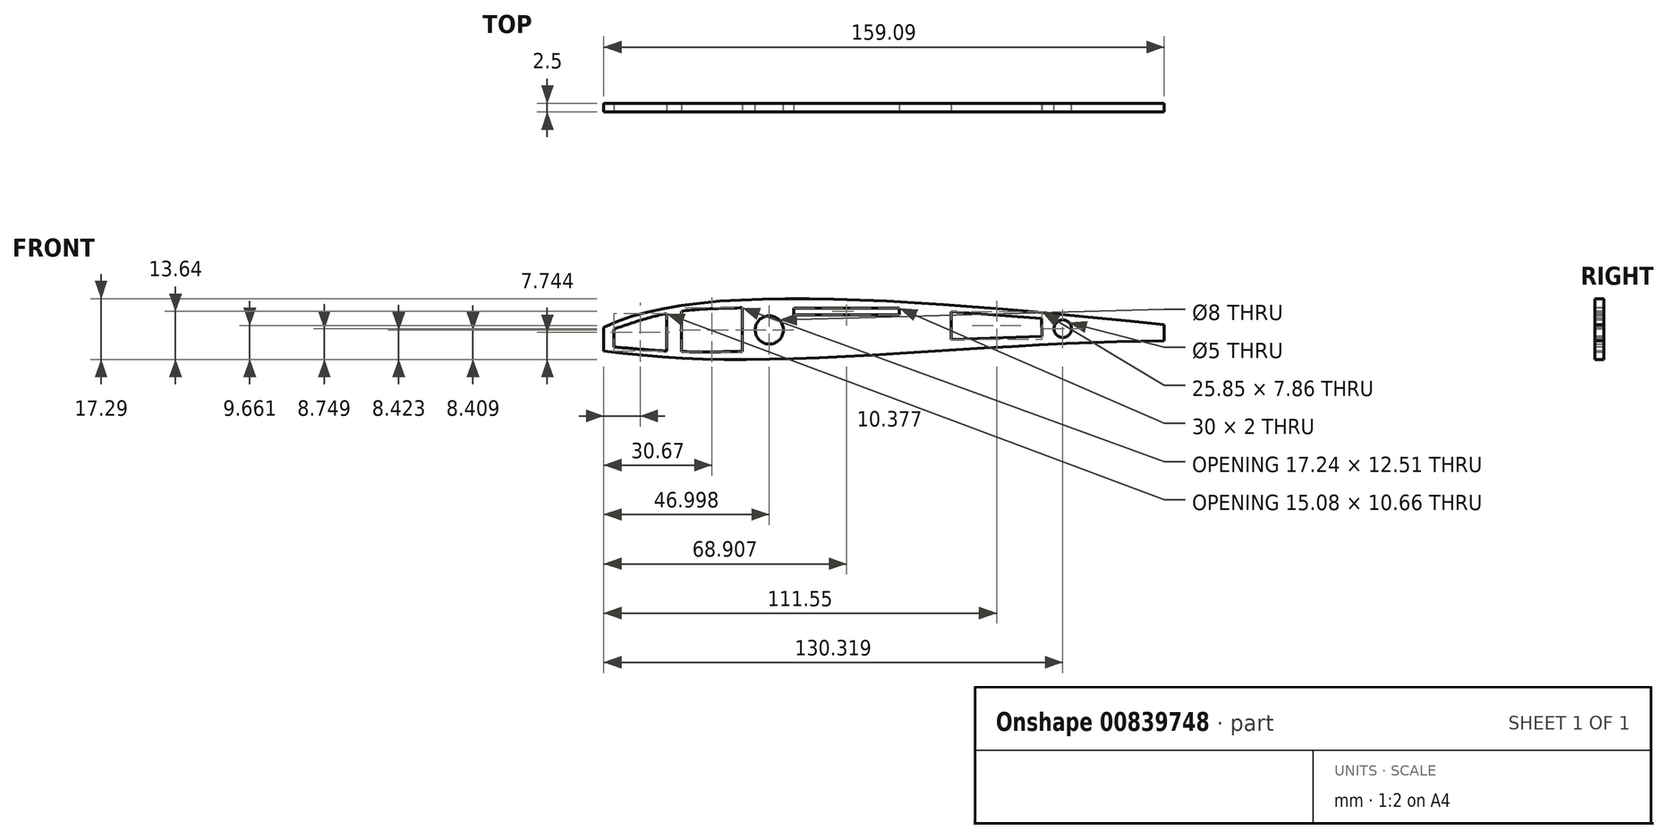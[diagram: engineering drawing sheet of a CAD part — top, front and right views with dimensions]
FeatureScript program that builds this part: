
annotation { "Feature Type Name" : "Feature", "Feature Type Description" : "" }
export const myFeature = defineFeature(function(context is Context, id is Id, definition is map)
    precondition{}
    {
        {
            var Q0;
            Q0=qCreatedBy(makeId("Front.planeOp"),FACE);
            var sketch = newSketch(context, id + "F0", { "sketchPlane" : qUnion([Q0])});
            skPoint(sketch, "E0.middle", {"position": v(0, 0) * mm});
            skLineSegment(sketch, "E1", {"start": v(-99.95, -4.05) * mm, "end": v(-99.64, -4.05) * mm});
            skFitSpline(sketch, "E2", {"points": [v(-96.98, -0.81) * mm, v(-45.24, 7.5) * mm, v(100, -4.05) * mm], "startDerivative": vector(97.58, 47.67) * mm, "endDerivative": vector(275.05, -31.29) * mm});
            skFitSpline(sketch, "E3", {"points": [v(-96.54, -7.34) * mm, v(-44.56, -9.6) * mm, v(41.7, -4.97) * mm, v(100, -4.05) * mm], "startDerivative": vector(159.07, -20.98) * mm, "endDerivative": vector(169.88, 6) * mm});
            skFitSpline(sketch, "E4", {"points": [v(-96.54, -7.34) * mm, v(-101.41, -5) * mm, v(-96.98, -0.81) * mm], "startDerivative": vector(-18.7, 3.9) * mm, "endDerivative": vector(17.62, 9.13) * mm});
            skArc(sketch, "E5.trimOffspring", {"start": v(-97.54, -7.12) * mm, "mid": v(-97.05, -7.27) * mm, "end": v(-96.54, -7.34) * mm});
            skFitSpline(sketch, "E6", {"points": [v(-96.34, -1.64) * mm, v(-45.34, 6.27) * mm, v(86.1, -3.38) * mm], "startDerivative": vector(82.57, 38.4) * mm, "endDerivative": vector(239.73, -24.74) * mm});
            skFitSpline(sketch, "E7", {"points": [v(-97.38, -6.05) * mm, v(-44.49, -7.96) * mm, v(41.39, -3.9) * mm, v(86.1, -3.38) * mm], "startDerivative": vector(144.05, -26.77) * mm, "endDerivative": vector(139.27, -2.3) * mm});
            skFitSpline(sketch, "E8", {"points": [v(-97.38, -6.05) * mm, v(-99.95, -4.56) * mm, v(-96.34, -1.64) * mm], "startDerivative": vector(-8.62, 1.03) * mm, "endDerivative": vector(10.24, 4.38) * mm});
            skSolve(sketch);
        }
        {
            var Q0;
            Q0=qCreatedBy(makeId("Front.planeOp"),FACE);
            var sketch = newSketch(context, id + "F1", { "sketchPlane" : qUnion([Q0])});
            skLineSegment(sketch, "E9", {"start": v(-109.84, -5.04) * mm, "end": v(108.45, -3.99) * mm});
            skCircle(sketch, "E10", {"center": v(-49.54, -1.37) * mm, "radius": 4 * mm});
            skCircle(sketch, "E11", {"center": v(33.78, -1.03) * mm, "radius": 2.5 * mm});
            skSolve(sketch);
        }
        {
            var Q0;
            {var subQ0=sQuery(id+"F0.wireOp",EDGE,"E6");Q0=makeQuery(id+"F0.imprint","IMPRINT",FACE,{"disambiguationData":[TD([[makeQuery(id+"F0.imprint","IMPRINT",EDGE,{"derivedFrom":subQ0}),-1.0]])]});}
            var Q1;
            {var subQ1=sQuery(id+"F0.wireOp",EDGE,"E2");Q1=makeQuery(id+"F0.imprint","IMPRINT",FACE,{"disambiguationData":[TD([[makeQuery(id+"F0.imprint","IMPRINT",EDGE,{"derivedFrom":subQ1}),-1.0]])]});}
            var Q2;
            Q2=makeQuery(id+"F1.imprint","IMPRINT",FACE,{"disambiguationData":[TD([[makeQuery(id+"F1.imprint","IMPRINT",EDGE,{"derivedFrom":sQuery(id+"F1.wireOp",EDGE,"E11")}),1.0]])]});
            var Q3;
            {var subQ0=sQuery(id+"F1.wireOp",EDGE,"E10");var subQ1=sQuery(id+"F1.wireOp",EDGE,"E9");var subQ2=makeQuery(id+"F1.imprint","INTERSECT",VERTEX,{"disambiguationData":[OD(0.0)],"derivedFrom":[subQ1,subQ0]});Q3=makeQuery(id+"F1.imprint","IMPRINT",FACE,{"disambiguationData":[TD([[makeQuery(id+"F1.imprint","IMPRINT",EDGE,{"disambiguationData":[TD([[subQ2,-1.0]])],"derivedFrom":subQ1}),1.0]])]});}
            var Q4;
            {var subQ0=sQuery(id+"F1.wireOp",EDGE,"E10");var subQ1=sQuery(id+"F1.wireOp",EDGE,"E9");var subQ2=makeQuery(id+"F1.imprint","INTERSECT",VERTEX,{"disambiguationData":[OD(0.0)],"derivedFrom":[subQ1,subQ0]});Q4=makeQuery(id+"F1.imprint","IMPRINT",FACE,{"disambiguationData":[TD([[makeQuery(id+"F1.imprint","IMPRINT",EDGE,{"disambiguationData":[TD([[subQ2,-1.0]])],"derivedFrom":subQ1}),-1.0]])]});}
            var Q5;
            {var subQ0=sQuery(id+"F0.wireOp",EDGE,"E5.trimOffspring");Q5=makeQuery(id+"F0.imprint","IMPRINT",FACE,{"disambiguationData":[TD([[makeQuery(id+"F0.imprint","IMPRINT",EDGE,{"derivedFrom":subQ0}),1.0]])]});}
            extrude(context, id + "F2", {"entities" : qUnion([Q0, Q1, Q2, Q3, Q4, Q5]), "depth" : 2.5 * mm, "offsetDistance" : 25 * mm});
        }
        {
            var Q0;
            Q0 = qSketchRegion(id + "F1", true);
            var Q1;
            Q1=sQuery(id+"F1.wireOp",EDGE,"E11");
            var Q2;
            Q2=sQuery(id+"F1.wireOp",EDGE,"E10");
            extrude(context, id + "F3", {"entities" : qUnion([Q0]), "operationType" : NewBodyOperationType.REMOVE, "surfaceEntities" : qUnion([Q1, Q2]), "depth" : 2.5 * mm, "offsetDistance" : 25 * mm});
        }
        {
            var Q0;
            Q0=makeQuery(id+"F2.opExtrude","CAP_FACE",FACE,{"disambiguationData":[OSD([sQuery(id+"F0.wireOp",EDGE,"E2"),sQuery(id+"F0.wireOp",EDGE,"E3"),sQuery(id+"F0.wireOp",EDGE,"E4"),sQuery(id+"F0.wireOp",EDGE,"E5.trimOffspring")])],"isStart":false});
            var sketch = newSketch(context, id + "F4", { "sketchPlane" : qUnion([Q0])});
            skLineSegment(sketch, "E12", {"start": v(-96.54, -0.6) * mm, "end": v(-96.54, -7.34) * mm});
            skPoint(sketch, "E13.end.orphan", {"position": v(-96.98, -7.34) * mm});
            skLineSegment(sketch, "E14", {"start": v(-57.25, 4.9) * mm, "end": v(-57.25, -7.48) * mm});
            skFitSpline(sketch, "E15", {"points": [v(-57.25, -7.48) * mm, v(-75.97, -7.48) * mm, v(-93.7, -6.2) * mm], "startDerivative": vector(-37.23, -0.66) * mm, "endDerivative": vector(-35.67, 3.25) * mm});
            skFitSpline(sketch, "E16", {"points": [v(-57.25, 4.9) * mm, v(-77.46, 3.51) * mm, v(-93.7, -1.14) * mm], "startDerivative": vector(-39.88, -0.8) * mm, "endDerivative": vector(-32.92, -11.45) * mm});
            skLineSegment(sketch, "E17", {"start": v(-93.7, -1.14) * mm, "end": v(-93.7, -6.2) * mm});
            skLineSegment(sketch, "E18", {"start": v(2.08, 3.8) * mm, "end": v(2.08, -4.05) * mm});
            skLineSegment(sketch, "E19", {"start": v(2.08, -4.05) * mm, "end": v(27.94, -3.22) * mm});
            skLineSegment(sketch, "E20", {"start": v(27.94, -3.22) * mm, "end": v(27.77, 1.91) * mm});
            skLineSegment(sketch, "E21", {"start": v(27.77, 1.91) * mm, "end": v(2.08, 3.8) * mm});
            skLineSegment(sketch, "E22", {"start": v(-78.62, 3.3) * mm, "end": v(-78.62, -7.37) * mm});
            skLineSegment(sketch, "E23", {"start": v(-74.49, 3.96) * mm, "end": v(-74.49, -7.53) * mm});
            skPoint(sketch, "E24.end.orphan", {"position": v(-41.2, -6.73) * mm});
            skLineSegment(sketch, "E25.bottom", {"start": v(-42.63, 4.86) * mm, "end": v(-12.63, 4.86) * mm});
            skLineSegment(sketch, "E25.top", {"start": v(-42.63, 2.86) * mm, "end": v(-12.63, 2.86) * mm});
            skLineSegment(sketch, "E25.left", {"start": v(-42.63, 4.86) * mm, "end": v(-42.63, 2.86) * mm});
            skLineSegment(sketch, "E25.right", {"start": v(-12.63, 4.86) * mm, "end": v(-12.63, 2.86) * mm});
            skLineSegment(sketch, "E26", {"start": v(62.55, 0.1) * mm, "end": v(62.55, -4.52) * mm});
            skSolve(sketch);
        }
        {
            var Q0;
            {var subQ0=sQuery(id+"F4.wireOp",EDGE,"E12");Q0=makeQuery(id+"F4.imprint","IMPRINT",FACE,{"disambiguationData":[TD([[makeQuery(id+"F4.imprint","IMPRINT",EDGE,{"derivedFrom":subQ0}),-1.0]])]});}
            extrude(context, id + "F5", {"entities" : qUnion([Q0]), "operationType" : NewBodyOperationType.REMOVE, "oppositeDirection" : true, "depth" : 2.5 * mm, "offsetDistance" : 25 * mm});
        }
        {
            var Q0;
            Q0=makeQuery(id+"F4.imprint","IMPRINT",FACE,{"disambiguationData":[TD([[makeQuery(id+"F4.imprint","IMPRINT",EDGE,{"derivedFrom":sQuery(id+"F4.wireOp",EDGE,"E17")}),1.0]])]});
            var Q1;
            Q1=makeQuery(id+"F4.imprint","IMPRINT",FACE,{"disambiguationData":[TD([[makeQuery(id+"F4.imprint","IMPRINT",EDGE,{"derivedFrom":sQuery(id+"F4.wireOp",EDGE,"E14")}),-1.0]])]});
            var Q2;
            Q2=makeQuery(id+"F4.imprint","IMPRINT",FACE,{"disambiguationData":[TD([[makeQuery(id+"F4.imprint","IMPRINT",EDGE,{"derivedFrom":sQuery(id+"F4.wireOp",EDGE,"E25.bottom")}),-1.0]])]});
            var Q3;
            Q3=makeQuery(id+"F4.imprint","IMPRINT",FACE,{"disambiguationData":[TD([[makeQuery(id+"F4.imprint","IMPRINT",EDGE,{"derivedFrom":sQuery(id+"F4.wireOp",EDGE,"E18")}),1.0]])]});
            extrude(context, id + "F6", {"entities" : qUnion([Q0, Q1, Q2, Q3]), "operationType" : NewBodyOperationType.REMOVE, "oppositeDirection" : true, "depth" : 2.5 * mm, "offsetDistance" : 25 * mm});
        }
        {
            var Q0;
            {var subQ0=sQuery(id+"F4.wireOp",EDGE,"E26");Q0=makeQuery(id+"F4.imprint","IMPRINT",FACE,{"disambiguationData":[TD([[makeQuery(id+"F4.imprint","IMPRINT",EDGE,{"derivedFrom":subQ0}),1.0]])]});}
            extrude(context, id + "F7", {"entities" : qUnion([Q0]), "operationType" : NewBodyOperationType.REMOVE, "oppositeDirection" : true, "depth" : 2.5 * mm, "offsetDistance" : 25 * mm});
        }
    });
